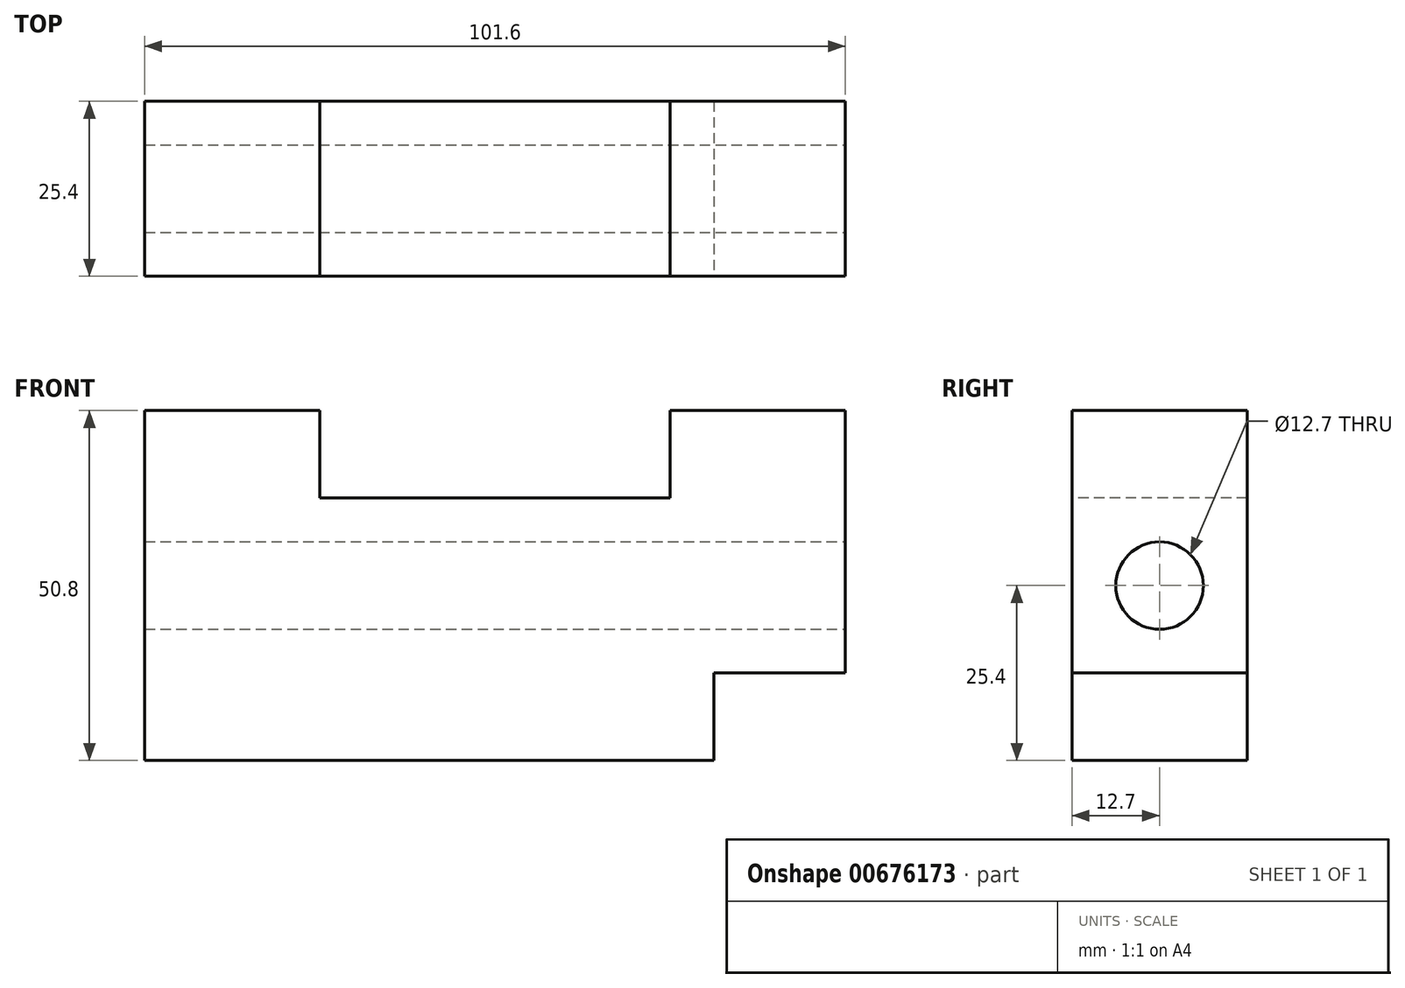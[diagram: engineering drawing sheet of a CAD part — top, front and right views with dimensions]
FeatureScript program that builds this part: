
annotation { "Feature Type Name" : "Feature", "Feature Type Description" : "" }
export const myFeature = defineFeature(function(context is Context, id is Id, definition is map)
    precondition{}
    {
        {
            var Q0;
            Q0=qCreatedBy(makeId("Front.planeOp"),FACE);
            var sketch = newSketch(context, id + "F0", { "sketchPlane" : qUnion([Q0])});
            skLineSegment(sketch, "E0.bottom", {"start": v(-50.8, 25.4) * mm, "end": v(50.8, 25.4) * mm});
            skLineSegment(sketch, "E0.top", {"start": v(-50.8, -25.4) * mm, "end": v(50.8, -25.4) * mm});
            skLineSegment(sketch, "E0.left", {"start": v(-50.8, 25.4) * mm, "end": v(-50.8, -25.4) * mm});
            skLineSegment(sketch, "E0.right", {"start": v(50.8, 25.4) * mm, "end": v(50.8, -25.4) * mm});
            skPoint(sketch, "E0.middle", {"position": v(0, 0) * mm});
            skSolve(sketch);
        }
        {
            var Q0;
            Q0 = qSketchRegion(id + "F0", true);
            extrude(context, id + "F1", {"entities" : qUnion([Q0]), "depth" : 25.4 * mm, "offsetDistance" : 25.4 * mm});
        }
        {
            var Q0;
            Q0=makeQuery(id+"F1.opExtrude","CAP_FACE",FACE,{"disambiguationData":[OSD([sQuery(id+"F0.wireOp",EDGE,"E0.bottom"),sQuery(id+"F0.wireOp",EDGE,"E0.top"),sQuery(id+"F0.wireOp",EDGE,"E0.left"),sQuery(id+"F0.wireOp",EDGE,"E0.right")])],"isStart":false});
            var sketch = newSketch(context, id + "F2", { "sketchPlane" : qUnion([Q0])});
            skLineSegment(sketch, "E1.bottom", {"start": v(-25.4, 25.4) * mm, "end": v(25.4, 25.4) * mm});
            skLineSegment(sketch, "E1.top", {"start": v(-25.4, 12.7) * mm, "end": v(25.4, 12.7) * mm});
            skLineSegment(sketch, "E1.left", {"start": v(-25.4, 25.4) * mm, "end": v(-25.4, 12.7) * mm});
            skLineSegment(sketch, "E1.right", {"start": v(25.4, 25.4) * mm, "end": v(25.4, 12.7) * mm});
            skLineSegment(sketch, "E2.bottom", {"start": v(31.75, -25.4) * mm, "end": v(50.8, -25.4) * mm});
            skLineSegment(sketch, "E2.top", {"start": v(31.75, -12.7) * mm, "end": v(50.8, -12.7) * mm});
            skLineSegment(sketch, "E2.left", {"start": v(31.75, -25.4) * mm, "end": v(31.75, -12.7) * mm});
            skLineSegment(sketch, "E2.right", {"start": v(50.8, -25.4) * mm, "end": v(50.8, -12.7) * mm});
            skSolve(sketch);
        }
        {
            var Q0;
            Q0=makeQuery(id+"F2.imprint","IMPRINT",FACE,{"disambiguationData":[TD([[makeQuery(id+"F2.imprint","IMPRINT",EDGE,{"derivedFrom":sQuery(id+"F2.wireOp",EDGE,"E1.bottom")}),-1.0]])]});
            extrude(context, id + "F3", {"entities" : qUnion([Q0]), "operationType" : NewBodyOperationType.REMOVE, "oppositeDirection" : true, "depth" : 25.4 * mm, "offsetDistance" : 25.4 * mm});
        }
        {
            var Q0;
            Q0=makeQuery(id+"F2.imprint","IMPRINT",FACE,{"disambiguationData":[TD([[makeQuery(id+"F2.imprint","IMPRINT",EDGE,{"derivedFrom":sQuery(id+"F2.wireOp",EDGE,"E2.bottom")}),1.0]])]});
            extrude(context, id + "F4", {"entities" : qUnion([Q0]), "operationType" : NewBodyOperationType.REMOVE, "oppositeDirection" : true, "depth" : 25.4 * mm, "offsetDistance" : 25.4 * mm});
        }
        {
            var Q0;
            Q0=makeQuery(id+"F1.opExtrude","SWEPT_FACE",FACE,{"disambiguationData":[OSD([sQuery(id+"F0.wireOp",EDGE,"E0.right")])]});
            var sketch = newSketch(context, id + "F5", { "sketchPlane" : qUnion([Q0])});
            skCircle(sketch, "E3", {"center": v(-12.7, 0) * mm, "radius": 6.35 * mm});
            skSolve(sketch);
        }
        {
            var Q0;
            Q0=makeQuery(id+"F5.imprint","IMPRINT",FACE,{"disambiguationData":[TD([[makeQuery(id+"F5.imprint","IMPRINT",EDGE,{"derivedFrom":sQuery(id+"F5.wireOp",EDGE,"E3")}),1.0]])]});
            extrude(context, id + "F6", {"entities" : qUnion([Q0]), "operationType" : NewBodyOperationType.REMOVE, "oppositeDirection" : true, "depth" : 25.4 * mm, "offsetDistance" : 25.4 * mm});
        }
        {
            var Q0;
            Q0=makeQuery(id+"F5.imprint","IMPRINT",FACE,{"disambiguationData":[TD([[makeQuery(id+"F5.imprint","IMPRINT",EDGE,{"derivedFrom":sQuery(id+"F5.wireOp",EDGE,"E3")}),1.0]])]});
            extrude(context, id + "F7", {"entities" : qUnion([Q0]), "operationType" : NewBodyOperationType.REMOVE, "oppositeDirection" : true, "depth" : 101.6 * mm, "offsetDistance" : 25.4 * mm});
        }
    });
